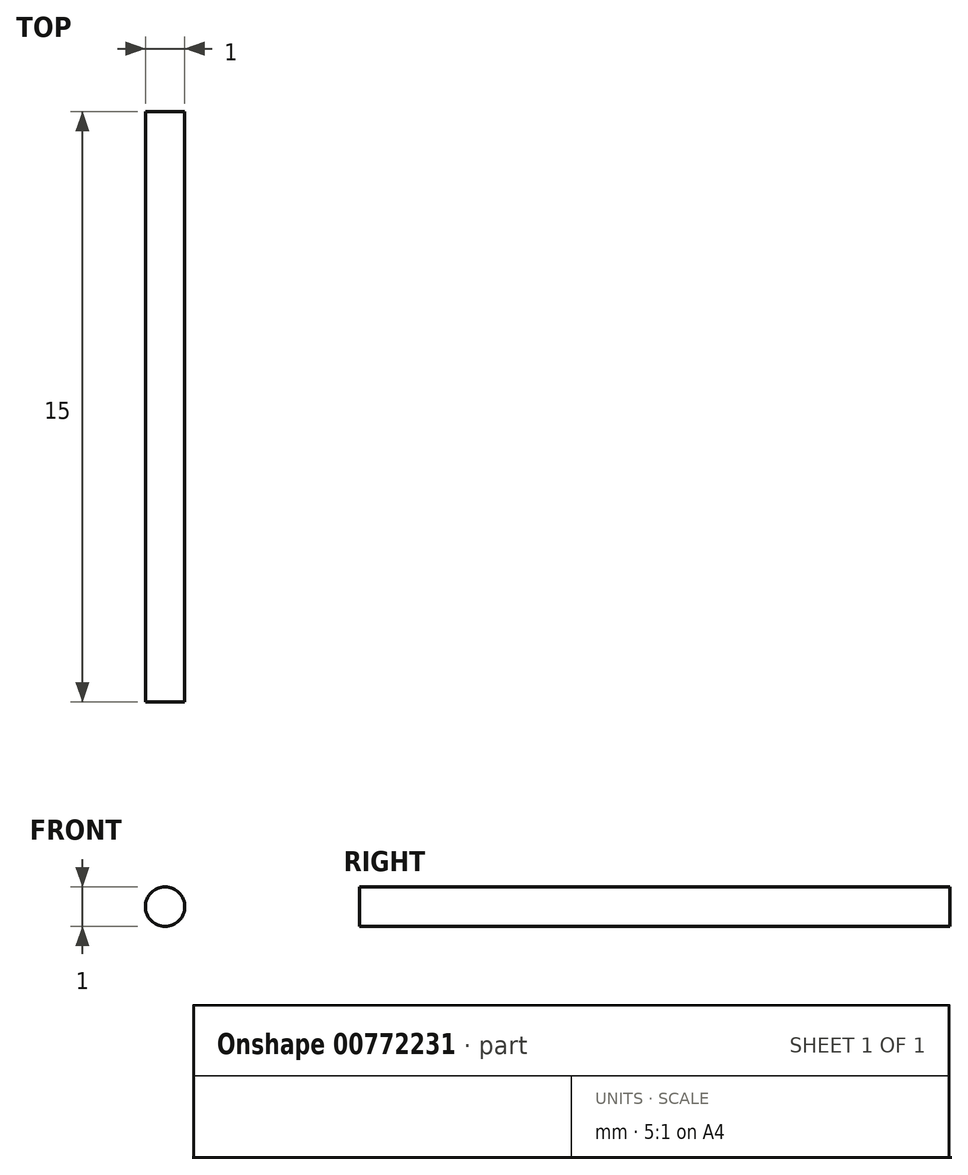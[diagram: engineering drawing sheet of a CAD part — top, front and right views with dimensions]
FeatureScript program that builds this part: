
annotation { "Feature Type Name" : "Feature", "Feature Type Description" : "" }
export const myFeature = defineFeature(function(context is Context, id is Id, definition is map)
    precondition{}
    {
        {
            var Q0;
            Q0=qCreatedBy(makeId("Front.planeOp"),FACE);
            var sketch = newSketch(context, id + "F0", { "sketchPlane" : qUnion([Q0])});
            skCircle(sketch, "E0", {"center": v(0, 0) * mm, "radius": 0.5 * mm});
            skSolve(sketch);
        }
        {
            var Q0;
            Q0 = qSketchRegion(id + "F0", true);
            extrude(context, id + "F1", {"entities" : qUnion([Q0]), "depth" : 15 * mm, "offsetDistance" : 25 * mm});
        }
    });
